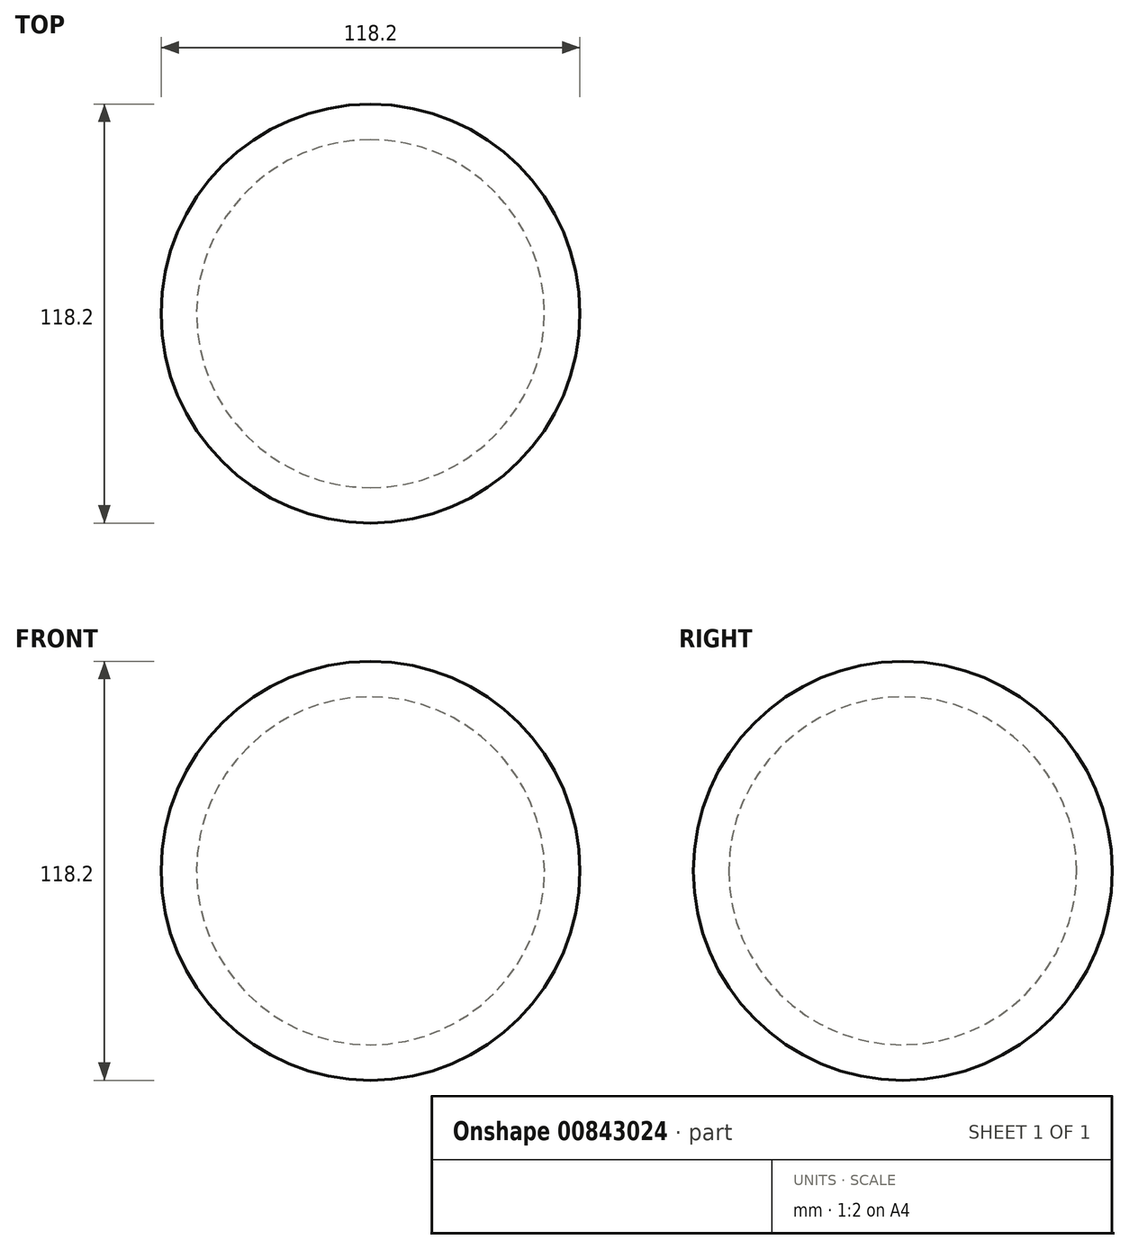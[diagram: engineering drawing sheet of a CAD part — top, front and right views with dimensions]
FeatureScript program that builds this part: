
annotation { "Feature Type Name" : "Feature", "Feature Type Description" : "" }
export const myFeature = defineFeature(function(context is Context, id is Id, definition is map)
    precondition{}
    {
        {
            var Q0;
            Q0=qCreatedBy(makeId("Top.planeOp"),FACE);
            var sketch = newSketch(context, id + "F0", { "sketchPlane" : qUnion([Q0])});
            skArc(sketch, "E0", {"start": v(0, -49.1) * mm, "mid": v(49.1, 0) * mm, "end": v(0, 49.1) * mm});
            skArc(sketch, "E1.0", {"start": v(0, -59.1) * mm, "mid": v(59.1, 0) * mm, "end": v(0, 59.1) * mm});
            skLineSegment(sketch, "E2", {"start": v(0, 59.1) * mm, "end": v(0, -59.1) * mm});
            skSolve(sketch);
        }
        {
            var Q0;
            {var subQ0=sQuery(id+"F0.wireOp",EDGE,"E0");Q0=makeQuery(id+"F0.imprint","IMPRINT",FACE,{"disambiguationData":[TD([[makeQuery(id+"F0.imprint","IMPRINT",EDGE,{"derivedFrom":subQ0}),-1.0]])]});}
            var Q1;
            Q1=sQuery(id+"F0.wireOp",EDGE,"E2");
            revolve(context, id + "F1", {"surfaceOperationType" : NewSurfaceOperationType.NEW, "entities" : qUnion([Q0]), "axis" : qUnion([Q1]), "revolveType" : RevolveType.FULL});
        }
    });
